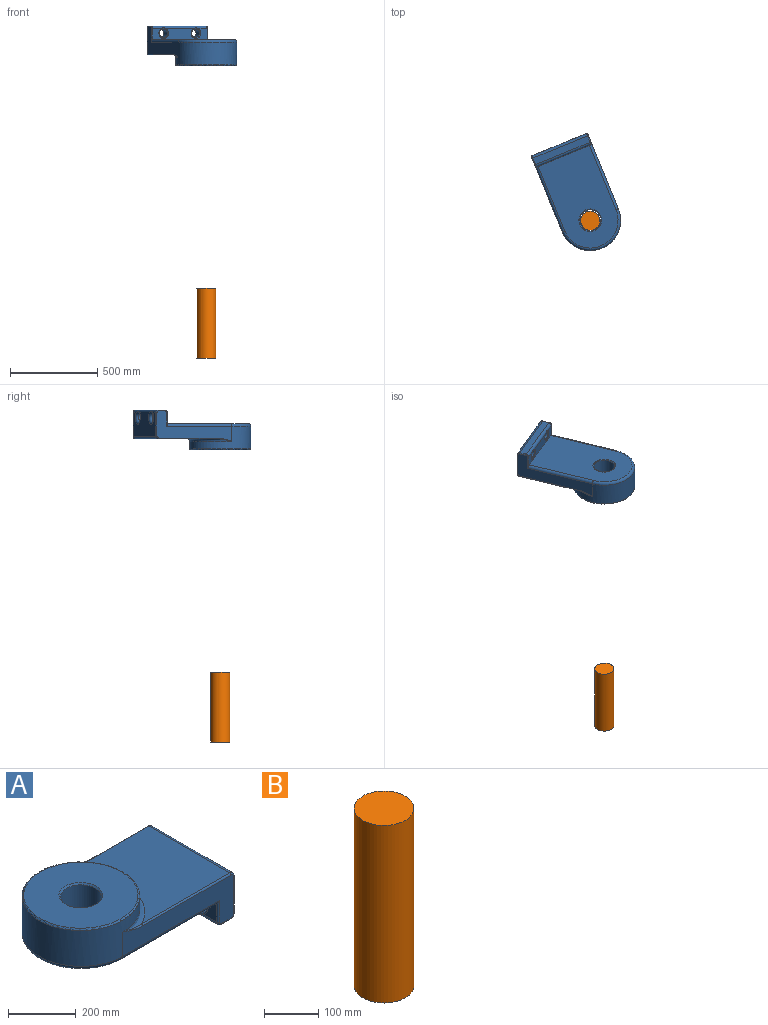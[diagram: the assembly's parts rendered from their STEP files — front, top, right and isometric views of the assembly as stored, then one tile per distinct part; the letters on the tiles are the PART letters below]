
ASSEMBLY  parts=2 mates=2
PART A: 44 faces, bbox 660.1x433.3x240.8 mm
  f0: plane 465x176.16mm, normal (0,1,0), area 37494.8mm2, adj f1,f14,f30,f31,f32,f33,f34,f35
  f1: cylinder r=174.52mm len=349.03mm, axis (0,0,-1), area 94300.6mm2, adj f0,f2,f13,f20,f42
  f2: plane 465x176.16mm, normal (0,-1,0), area 37494.8mm2, adj f1,f12,f22,f23,f24,f25,f26,f27
  f3: cylinder r=60mm len=140mm, axis (0,0,-1), area 52778.8mm2, adj f21,f43
  f4: plane 370.26x339.03mm, normal (0,0,1), area 100127.1mm2, adj f19,f20,f23,f31
  f5: plane 559.52x319.03mm, normal (0,0,-1), area 154309.5mm2, adj f11,f12,f13,f14,f43
  f6: plane 339.03x339.03mm, normal (0,0,1), area 77002.9mm2, adj f21,f42
  f7: cylinder r=24.76mm len=50mm, axis (-1,0,0), area 7774.7mm2, adj f16,f40,f41
  f8: plane 339.03x40mm, normal (0,0,-1), area 13561.3mm2, adj f15,f17,f27,f35
  f9: cylinder r=24.76mm len=50mm, axis (-1,0,0), area 7774.7mm2, adj f18,f38,f39
  f10: plane 339.03x136.16mm, normal (1,0,0), area 37267.2mm2, adj f16,f17,f18,f19,f25,f33
  f11: plane 339.03x66.98mm, normal (-1,0,0), area 15967.9mm2, adj f5,f12,f14,f15,f29,f37,f38,f40
  f12: cylinder r=15mm len=405mm, axis (1,0,0), area 9448.9mm2, adj f2,f5,f11,f13,f29
  f13: torus R=159.52mm, axis (0,0,1), area 12514.6mm2, adj f1,f5,f12,f14
  f14: cylinder r=15mm len=405mm, axis (-1,0,0), area 9448.9mm2, adj f0,f5,f11,f13,f37
  f15: cylinder r=15mm len=339.03mm, axis (0,1,0), area 7841.5mm2, adj f8,f11,f28,f36,f39,f41
  f16: torus R=39.76mm, axis (1,0,0), area 4197.8mm2, adj f7,f10,f17
  f17: cylinder r=15mm len=339.03mm, axis (0,-1,0), area 7476.2mm2, adj f8,f10,f16,f18,f26,f34
  f18: torus R=39.76mm, axis (1,0,0), area 4197.8mm2, adj f9,f10,f17
  f19: cylinder r=15mm len=339.03mm, axis (0,-1,0), area 7988.3mm2, adj f4,f10,f24,f32
  f20: torus R=189.52mm, axis (0,0,1), area 11174.1mm2, adj f1,f4,f22,f30
  f21: cone r=60mm half-angle=45deg, axis (0,0,1), area 2776.8mm2, adj f3,f6
  f22: bspline ~91.48x20mm, area 330.6mm2, adj f2,f20,f23
  f23: cylinder r=5mm len=370.26mm, axis (-1,0,0), area 2908mm2, adj f2,f4,f22,f24
  f24: torus R=10mm, axis (0,1,0), area 162.6mm2, adj f2,f19,f23,f25
  f25: cylinder r=5mm len=136.16mm, axis (0,0,1), area 1069.4mm2, adj f2,f10,f24,f26
  f26: torus R=10mm, axis (0,1,0), area 162.6mm2, adj f2,f17,f25,f27
  f27: cylinder r=5mm len=40mm, axis (1,0,0), area 314.2mm2, adj f2,f8,f26,f28
  f28: torus R=10mm, axis (0,1,0), area 162.6mm2, adj f2,f15,f27,f29
  f29: cylinder r=5mm len=78.16mm, axis (0,0,-1), area 565.4mm2, adj f2,f11,f12,f28
  f30: bspline ~91.48x20mm, area 330.6mm2, adj f0,f20,f31
  f31: cylinder r=5mm len=370.26mm, axis (1,0,0), area 2908mm2, adj f0,f4,f30,f32
  f32: torus R=10mm, axis (0,1,0), area 162.6mm2, adj f0,f19,f31,f33
  f33: cylinder r=5mm len=136.16mm, axis (0,0,-1), area 1069.4mm2, adj f0,f10,f32,f34
  f34: torus R=10mm, axis (0,1,0), area 162.6mm2, adj f0,f17,f33,f35
  f35: cylinder r=5mm len=40mm, axis (-1,0,0), area 314.2mm2, adj f0,f8,f34,f36
  f36: torus R=10mm, axis (0,1,0), area 162.6mm2, adj f0,f15,f35,f37
  f37: cylinder r=5mm len=78.16mm, axis (0,0,1), area 565.4mm2, adj f0,f11,f14,f36
  f38: torus R=29.76mm, axis (1,0,0), area 1127.8mm2, adj f9,f11,f39
  f39: bspline ~28.4x9.92mm, area 208.4mm2, adj f9,f15,f38
  f40: torus R=29.76mm, axis (1,0,0), area 1127.8mm2, adj f7,f11,f41
  f41: bspline ~28.4x9.92mm, area 208.4mm2, adj f7,f15,f40
  f42: torus R=169.52mm, axis (0,0,1), area 8522.4mm2, adj f1,f6
  f43: torus R=65mm, axis (0,0,1), area 3050.5mm2, adj f3,f5
PART B: 3 faces, bbox 110x110x400 mm
  f0: cylinder r=55mm len=400mm, axis (0,0,-1), area 138230.1mm2, adj f1,f2
  f1: plane 110x110mm, normal (0,0,1), area 9503.3mm2, adj f0
  f2: plane 110x110mm, normal (0,0,-1), area 9503.3mm2, adj f0
PLACE A rot(axis=(-0.56,-0.83,0),180deg) t=(99.18,574.57,1767.48)mm
PLACE B t=(263.49,244.42,-61.56)mm fixed
MATE revolute B.f0 <-> B.f0  axis (0,0,-1) through (263.49,244.42,138.44)mm
MATE cylindrical A.f1 <-> B.f0  axis (0,0,-1) through (263.49,244.42,1617.48)mm
